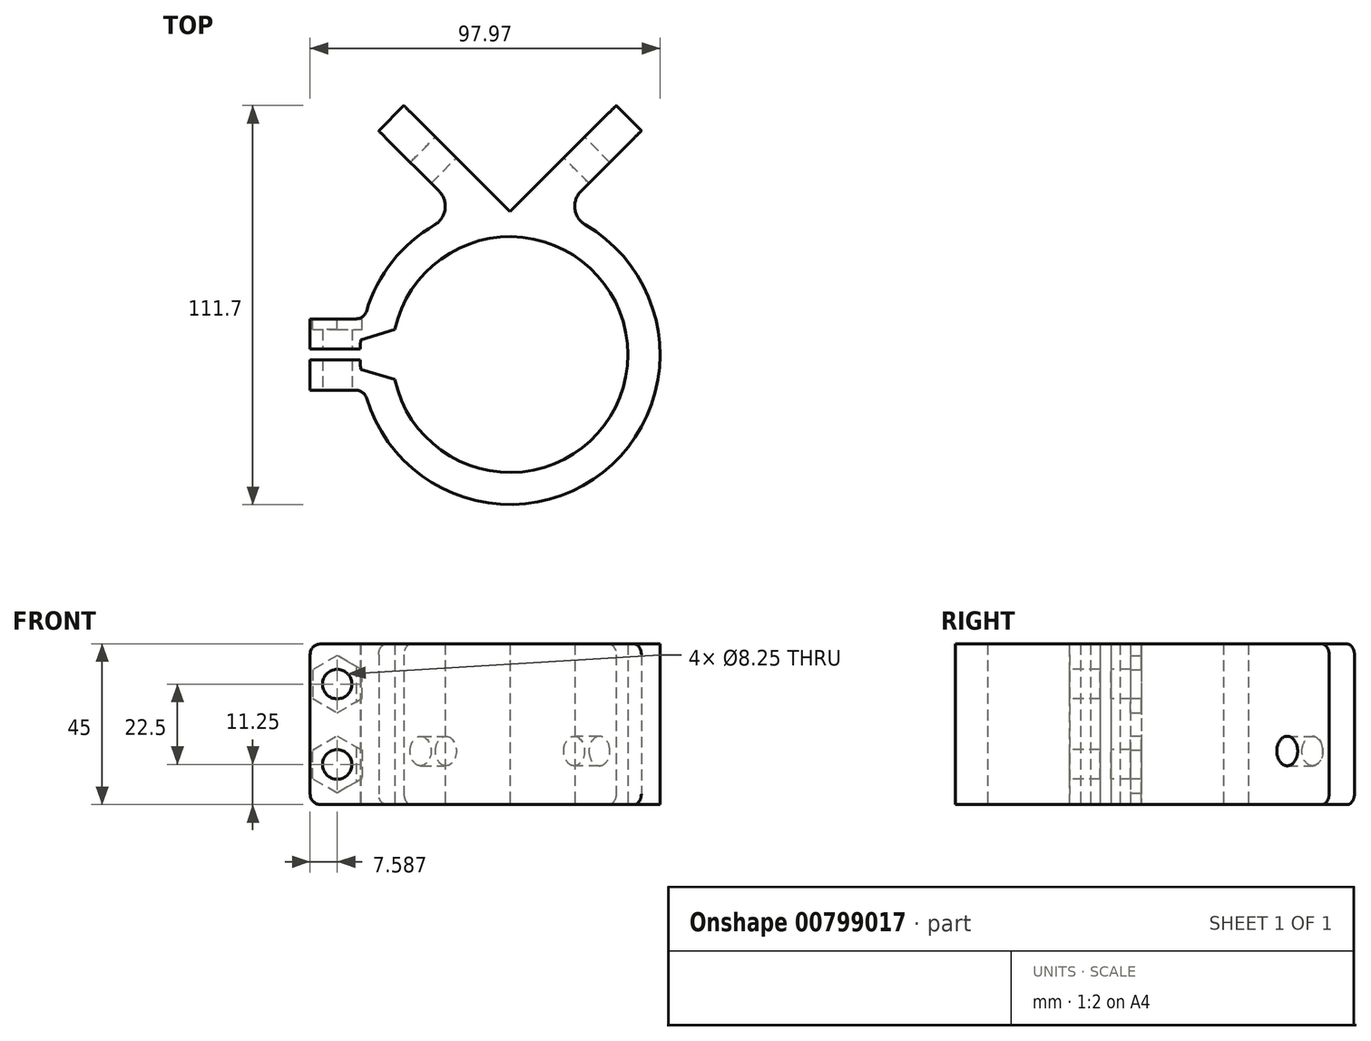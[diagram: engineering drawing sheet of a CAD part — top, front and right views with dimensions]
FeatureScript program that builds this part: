
annotation { "Feature Type Name" : "Feature", "Feature Type Description" : "" }
export const myFeature = defineFeature(function(context is Context, id is Id, definition is map)
    precondition{}
    {
        {
            var Q0;
            Q0=qCreatedBy(makeId("Top.planeOp"),FACE);
            var sketch = newSketch(context, id + "F0", { "sketchPlane" : qUnion([Q0])});
            skLineSegment(sketch, "E0", {"start": v(0, 0) * mm, "end": v(-29.7, 29.7) * mm});
            skLineSegment(sketch, "E1", {"start": v(0, 38.94) * mm, "end": v(0, 0) * mm, "construction": true});
            skLineSegment(sketch, "E2", {"start": v(-29.7, 29.7) * mm, "end": v(-36.77, 22.63) * mm});
            skLineSegment(sketch, "E3", {"start": v(-36.77, 22.63) * mm, "end": v(-13.8, -0.33) * mm});
            skLineSegment(sketch, "E4", {"start": v(0, 0) * mm, "end": v(0, -40) * mm, "construction": true});
            skArc(sketch, "E5", {"start": v(-32.97, -41.5) * mm, "mid": v(33, -40) * mm, "end": v(-32.97, -38.5) * mm});
            skArc(sketch, "E6", {"start": v(-41.97, -41.5) * mm, "mid": v(24.94, -73.8) * mm, "end": v(13.8, -0.33) * mm});
            skLineSegment(sketch, "E7", {"start": v(0, -40) * mm, "end": v(-42, -40) * mm, "construction": true});
            skLineSegment(sketch, "E8", {"start": v(-41.97, -38.5) * mm, "end": v(-55.97, -38.5) * mm});
            skLineSegment(sketch, "E9", {"start": v(-55.97, -38.5) * mm, "end": v(-55.97, -30) * mm});
            skLineSegment(sketch, "E10", {"start": v(-55.97, -30) * mm, "end": v(-40.8, -30) * mm});
            skLineSegment(sketch, "E11.MirrorCS", {"start": v(-55.97, -41.5) * mm, "end": v(-55.97, -50) * mm});
            skLineSegment(sketch, "E12.MirrorCS", {"start": v(-55.97, -50) * mm, "end": v(-40.8, -50) * mm});
            skLineSegment(sketch, "E13.MirrorCS", {"start": v(-41.97, -41.5) * mm, "end": v(-55.97, -41.5) * mm});
            skLineSegment(sketch, "E14", {"start": v(-41.97, -38.5) * mm, "end": v(-32.97, -38.5) * mm});
            skLineSegment(sketch, "E15.MirrorCS", {"start": v(-41.97, -41.5) * mm, "end": v(-32.97, -41.5) * mm});
            skLineSegment(sketch, "E16.MirrorCS", {"start": v(29.7, 29.7) * mm, "end": v(36.77, 22.63) * mm});
            skLineSegment(sketch, "E17.MirrorCS", {"start": v(0, 0) * mm, "end": v(29.7, 29.7) * mm});
            skLineSegment(sketch, "E18.MirrorCS", {"start": v(36.77, 22.63) * mm, "end": v(13.8, -0.33) * mm});
            skPoint(sketch, "E19.orphan", {"position": v(0, -14.14) * mm});
            skArc(sketch, "E20.trimOffspring", {"start": v(-13.8, -0.33) * mm, "mid": v(-33.8, -15.06) * mm, "end": v(-41.97, -38.5) * mm});
            skLineSegment(sketch, "E21", {"start": v(-32.25, -33) * mm, "end": v(-41.8, -35.88) * mm});
            skLineSegment(sketch, "E22", {"start": v(-41.8, -35.88) * mm, "end": v(-41.8, -41.5) * mm});
            skLineSegment(sketch, "E23.MirrorCS", {"start": v(-32.25, -47) * mm, "end": v(-41.8, -44.12) * mm});
            skLineSegment(sketch, "E24.MirrorCS", {"start": v(-41.8, -44.12) * mm, "end": v(-41.8, -38.5) * mm});
            skSolve(sketch);
        }
        {
            var Q0;
            Q0=makeQuery(id+"F0.imprint","IMPRINT",FACE,{"disambiguationData":[TD([[makeQuery(id+"F0.imprint","IMPRINT",EDGE,{"derivedFrom":sQuery(id+"F0.wireOp",EDGE,"E0")}),1.0]])]});
            var Q1;
            {var subQ4=sQuery(id+"F0.wireOp",EDGE,"E9");Q1=makeQuery(id+"F0.imprint","IMPRINT",FACE,{"disambiguationData":[TD([[makeQuery(id+"F0.imprint","IMPRINT",EDGE,{"derivedFrom":subQ4}),-1.0]])]});}
            var Q2;
            {var subQ1=sQuery(id+"F0.wireOp",EDGE,"E11.MirrorCS");Q2=makeQuery(id+"F0.imprint","IMPRINT",FACE,{"disambiguationData":[TD([[makeQuery(id+"F0.imprint","IMPRINT",EDGE,{"derivedFrom":subQ1}),1.0]])]});}
            extrude(context, id + "F1", {"entities" : qUnion([Q0, Q1, Q2]), "depth" : 45 * mm, "offsetDistance" : 25 * mm});
        }
        {
            var Q0;
            Q0=makeQuery(id+"F1.opExtrude","SWEPT_FACE",FACE,{"disambiguationData":[OSD([sQuery(id+"F0.wireOp",EDGE,"E17.MirrorCS")])]});
            var sketch = newSketch(context, id + "F2", { "sketchPlane" : qUnion([Q0])});
            skLineSegment(sketch, "E25", {"start": v(0, 15) * mm, "end": v(-50.8, 15) * mm, "construction": true});
            skCircle(sketch, "E26", {"center": v(-25.4, 15) * mm, "radius": 4.12 * mm});
            skSolve(sketch);
        }
        {
            var Q0;
            Q0=qSketchRegion(id+"F2",true);
            extrude(context, id + "F3", {"entities" : qUnion([Q0]), "operationType" : NewBodyOperationType.REMOVE, "endBound" : BoundingType.UP_TO_NEXT, "oppositeDirection" : true, "depth" : 25 * mm, "offsetDistance" : 25 * mm});
        }
        {
            var Q0;
            Q0=makeQuery(id+"F1.opExtrude","SWEPT_FACE",FACE,{"disambiguationData":[OSD([sQuery(id+"F0.wireOp",EDGE,"E0")])]});
            var sketch = newSketch(context, id + "F4", { "sketchPlane" : qUnion([Q0])});
            skLineSegment(sketch, "E27", {"start": v(0, 15) * mm, "end": v(50.8, 15) * mm, "construction": true});
            skCircle(sketch, "E28", {"center": v(25.4, 15) * mm, "radius": 4.12 * mm});
            skSolve(sketch);
        }
        {
            var Q0;
            Q0=qSketchRegion(id+"F4",true);
            extrude(context, id + "F5", {"entities" : qUnion([Q0]), "operationType" : NewBodyOperationType.REMOVE, "endBound" : BoundingType.UP_TO_NEXT, "oppositeDirection" : true, "depth" : 25 * mm, "offsetDistance" : 25 * mm});
        }
        {
            var Q0;
            Q0=makeQuery(id+"F1.opExtrude","SWEPT_FACE",FACE,{"disambiguationData":[OSD([sQuery(id+"F0.wireOp",EDGE,"E12.MirrorCS")])]});
            var sketch = newSketch(context, id + "F6", { "sketchPlane" : qUnion([Q0])});
            skLineSegment(sketch, "E29", {"start": v(-48.38, 45) * mm, "end": v(-48.38, 0) * mm, "construction": true});
            skLineSegment(sketch, "E30", {"start": v(-55.97, 22.5) * mm, "end": v(-40.8, 22.5) * mm, "construction": true});
            skLineSegment(sketch, "E31", {"start": v(-55.97, 22.5) * mm, "end": v(-40.8, 45) * mm, "construction": true});
            skCircle(sketch, "E32", {"center": v(-48.38, 33.75) * mm, "radius": 4.12 * mm});
            skCircle(sketch, "E33.MirrorC", {"center": v(-48.38, 11.25) * mm, "radius": 4.12 * mm});
            skLineSegment(sketch, "E34.MirrorCS", {"start": v(-55.97, 22.5) * mm, "end": v(-40.8, 0) * mm, "construction": true});
            skSolve(sketch);
        }
        {
            var Q0;
            Q0=qSketchRegion(id+"F6",true);
            var Q1;
            Q1=makeQuery(id+"F1.opExtrude","SWEPT_FACE",FACE,{"disambiguationData":[OSD([sQuery(id+"F0.wireOp",EDGE,"E10")])]});
            extrude(context, id + "F7", {"entities" : qUnion([Q0]), "operationType" : NewBodyOperationType.REMOVE, "endBound" : BoundingType.UP_TO_SURFACE, "oppositeDirection" : true, "depth" : 25 * mm, "endBoundEntityFace" : qUnion([Q1]), "offsetDistance" : 25 * mm});
        }
        {
            var Q0;
            Q0=makeQuery(id+"F1.opExtrude","CAP_EDGE",EDGE,{"disambiguationData":[OSD([sQuery(id+"F0.wireOp",EDGE,"E9")])],"isStart":false});
            var Q1;
            Q1=makeQuery(id+"F1.opExtrude","CAP_EDGE",EDGE,{"disambiguationData":[OSD([sQuery(id+"F0.wireOp",EDGE,"E11.MirrorCS")])],"isStart":false});
            var Q2;
            Q2=makeQuery(id+"F1.opExtrude","CAP_EDGE",EDGE,{"disambiguationData":[OSD([sQuery(id+"F0.wireOp",EDGE,"E11.MirrorCS")])],"isStart":true});
            var Q3;
            Q3=makeQuery(id+"F1.opExtrude","CAP_EDGE",EDGE,{"disambiguationData":[OSD([sQuery(id+"F0.wireOp",EDGE,"E9")])],"isStart":true});
            var Q4;
            Q4=makeQuery(id+"F1.opExtrude","CAP_EDGE",EDGE,{"disambiguationData":[OSD([sQuery(id+"F0.wireOp",EDGE,"E2")])],"isStart":false});
            var Q5;
            Q5=makeQuery(id+"F1.opExtrude","CAP_EDGE",EDGE,{"disambiguationData":[OSD([sQuery(id+"F0.wireOp",EDGE,"E16.MirrorCS")])],"isStart":false});
            var Q6;
            Q6=makeQuery(id+"F1.opExtrude","CAP_EDGE",EDGE,{"disambiguationData":[OSD([sQuery(id+"F0.wireOp",EDGE,"E16.MirrorCS")])],"isStart":true});
            var Q7;
            Q7=makeQuery(id+"F1.opExtrude","CAP_EDGE",EDGE,{"disambiguationData":[OSD([sQuery(id+"F0.wireOp",EDGE,"E2")])],"isStart":true});
            var Q8;
            Q8=makeQuery(id+"F1.opExtrude","SWEPT_EDGE",EDGE,{"disambiguationData":[OSD([sQuery(id+"F0.wireOp",EDGE,"E10"),sQuery(id+"F0.wireOp",EDGE,"E20.trimOffspring")])]});
            var Q9;
            Q9=makeQuery(id+"F1.opExtrude","SWEPT_EDGE",EDGE,{"disambiguationData":[OSD([sQuery(id+"F0.wireOp",EDGE,"E6"),sQuery(id+"F0.wireOp",EDGE,"E12.MirrorCS")])]});
            fillet(context, id + "F8", {"entities" : qUnion([Q0, Q1, Q2, Q3, Q4, Q5, Q6, Q7, Q8, Q9]), "radius" : 3 * mm, "tangentPropagation" : true, "allowEdgeOverflow" : false});
        }
        {
            var Q0;
            Q0=makeQuery(id+"F1.opExtrude","SWEPT_FACE",FACE,{"disambiguationData":[OSD([sQuery(id+"F0.wireOp",EDGE,"E10")])]});
            var sketch = newSketch(context, id + "F9", { "sketchPlane" : qUnion([Q0])});
            skCircle(sketch, "E35.cCircle", {"center": v(48.38, 33.75) * mm, "radius": 6.92 * mm, "construction": true});
            skLineSegment(sketch, "E35.0", {"start": v(48.38, 41.75) * mm, "end": v(55.3, 37.75) * mm});
            skLineSegment(sketch, "E35.1", {"start": v(55.3, 37.75) * mm, "end": v(55.3, 29.75) * mm});
            skLineSegment(sketch, "E35.2", {"start": v(55.3, 29.75) * mm, "end": v(48.38, 25.75) * mm});
            skLineSegment(sketch, "E35.3", {"start": v(48.38, 25.75) * mm, "end": v(41.46, 29.75) * mm});
            skLineSegment(sketch, "E35.4", {"start": v(41.46, 29.75) * mm, "end": v(41.46, 37.75) * mm});
            skLineSegment(sketch, "E35.5", {"start": v(41.46, 37.75) * mm, "end": v(48.38, 41.75) * mm});
            skPoint(sketch, "E35.0.midPoint", {"position": v(51.85, 39.75) * mm});
            skLineSegment(sketch, "E36", {"start": v(74.38, 22.5) * mm, "end": v(55.97, 22.5) * mm, "construction": true});
            skLineSegment(sketch, "E37.MirrorCS", {"start": v(55.3, 15.25) * mm, "end": v(48.38, 19.25) * mm});
            skLineSegment(sketch, "E38.MirrorCS", {"start": v(41.46, 15.25) * mm, "end": v(41.46, 7.25) * mm});
            skLineSegment(sketch, "E39.MirrorCS", {"start": v(48.38, 3.25) * mm, "end": v(55.3, 7.25) * mm});
            skLineSegment(sketch, "E40.MirrorCS", {"start": v(48.38, 19.25) * mm, "end": v(41.46, 15.25) * mm});
            skCircle(sketch, "E41.MirrorC", {"center": v(48.38, 11.25) * mm, "radius": 6.92 * mm, "construction": true});
            skLineSegment(sketch, "E42.MirrorCS", {"start": v(55.3, 7.25) * mm, "end": v(55.3, 15.25) * mm});
            skLineSegment(sketch, "E43.MirrorCS", {"start": v(41.46, 7.25) * mm, "end": v(48.38, 3.25) * mm});
            skPoint(sketch, "E44.MirrorP", {"position": v(51.85, 5.25) * mm});
            skSolve(sketch);
        }
        {
            var Q0;
            Q0=qSketchRegion(id+"F9",true);
            extrude(context, id + "F10", {"entities" : qUnion([Q0]), "operationType" : NewBodyOperationType.REMOVE, "oppositeDirection" : true, "depth" : 3 * mm, "offsetDistance" : 25 * mm});
        }
        {
            var Q0;
            Q0=makeQuery(id+"F1.opExtrude","SWEPT_EDGE",EDGE,{"disambiguationData":[OSD([sQuery(id+"F0.wireOp",EDGE,"E3"),sQuery(id+"F0.wireOp",EDGE,"E20.trimOffspring")])]});
            var Q1;
            Q1=makeQuery(id+"F1.opExtrude","SWEPT_EDGE",EDGE,{"disambiguationData":[OSD([sQuery(id+"F0.wireOp",EDGE,"E6"),sQuery(id+"F0.wireOp",EDGE,"E18.MirrorCS")])]});
            fillet(context, id + "F11", {"entities" : qUnion([Q0, Q1]), "radius" : 6 * mm, "tangentPropagation" : true, "allowEdgeOverflow" : false});
        }
    });
